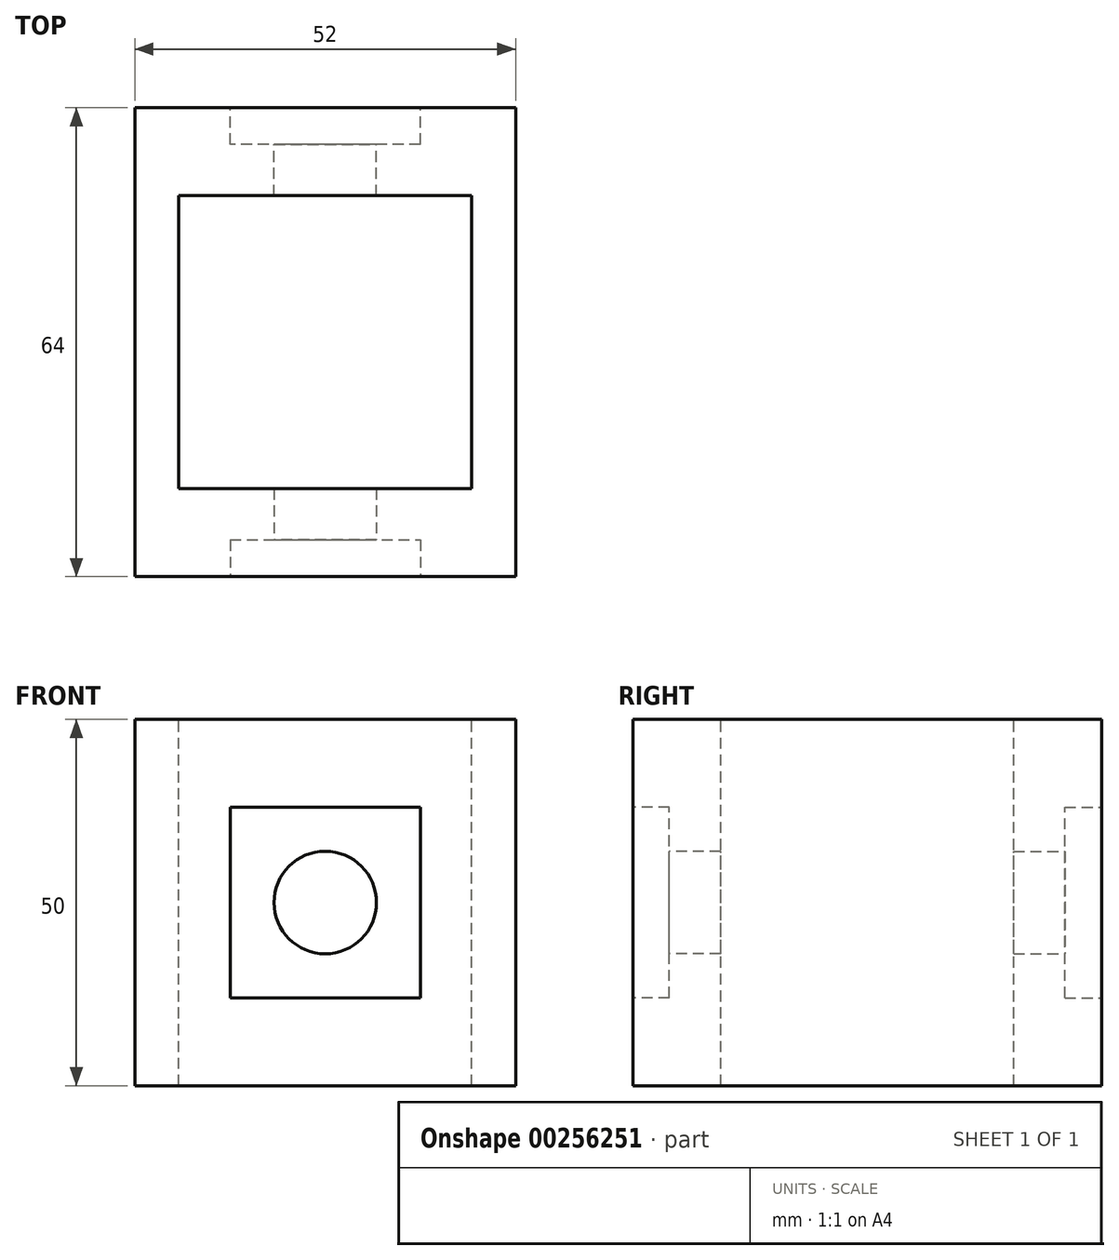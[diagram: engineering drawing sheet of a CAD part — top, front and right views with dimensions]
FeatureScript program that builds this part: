
annotation { "Feature Type Name" : "Feature", "Feature Type Description" : "" }
export const myFeature = defineFeature(function(context is Context, id is Id, definition is map)
    precondition{}
    {
        {
            var Q0;
            Q0=qCreatedBy(makeId("Top.planeOp"),FACE);
            var sketch = newSketch(context, id + "F0", { "sketchPlane" : qUnion([Q0])});
            skLineSegment(sketch, "E0.bottom", {"start": v(0, 0) * mm, "end": v(52, 0) * mm});
            skLineSegment(sketch, "E0.top", {"start": v(0, 64) * mm, "end": v(52, 64) * mm});
            skLineSegment(sketch, "E0.left", {"start": v(0, 0) * mm, "end": v(0, 64) * mm});
            skLineSegment(sketch, "E0.right", {"start": v(52, 0) * mm, "end": v(52, 64) * mm});
            skSolve(sketch);
        }
        {
            var Q0;
            Q0=makeQuery(id+"F0.imprint","IMPRINT",FACE,{"disambiguationData":[TD([[makeQuery(id+"F0.imprint","IMPRINT",EDGE,{"derivedFrom":sQuery(id+"F0.wireOp",EDGE,"E0.bottom")}),1.0]])]});
            extrude(context, id + "F1", {"entities" : qUnion([Q0]), "depth" : 50 * mm});
        }
        {
            var Q0;
            Q0=makeQuery(id+"F1.opExtrude","CAP_FACE",FACE,{"disambiguationData":[OSD([sQuery(id+"F0.wireOp",EDGE,"E0.bottom"),sQuery(id+"F0.wireOp",EDGE,"E0.top"),sQuery(id+"F0.wireOp",EDGE,"E0.left"),sQuery(id+"F0.wireOp",EDGE,"E0.right")])],"isStart":false});
            var sketch = newSketch(context, id + "F2", { "sketchPlane" : qUnion([Q0])});
            skLineSegment(sketch, "E1.bottom", {"start": v(6, 52) * mm, "end": v(46, 52) * mm});
            skLineSegment(sketch, "E1.top", {"start": v(6, 12) * mm, "end": v(46, 12) * mm});
            skLineSegment(sketch, "E1.left", {"start": v(6, 52) * mm, "end": v(6, 12) * mm});
            skLineSegment(sketch, "E1.right", {"start": v(46, 52) * mm, "end": v(46, 12) * mm});
            skSolve(sketch);
        }
        {
            var Q0;
            Q0=makeQuery(id+"F2.imprint","IMPRINT",FACE,{"disambiguationData":[TD([[makeQuery(id+"F2.imprint","IMPRINT",EDGE,{"derivedFrom":sQuery(id+"F2.wireOp",EDGE,"E1.bottom")}),-1.0]])]});
            extrude(context, id + "F3", {"entities" : qUnion([Q0]), "operationType" : NewBodyOperationType.REMOVE, "oppositeDirection" : true, "depth" : 50 * mm});
        }
        {
            var Q0;
            Q0=makeQuery(id+"F1.opExtrude","SWEPT_FACE",FACE,{"disambiguationData":[OSD([sQuery(id+"F0.wireOp",EDGE,"E0.bottom")])]});
            var sketch = newSketch(context, id + "F4", { "sketchPlane" : qUnion([Q0])});
            skLineSegment(sketch, "E2.bottom", {"start": v(13, 12) * mm, "end": v(39, 12) * mm});
            skLineSegment(sketch, "E2.top", {"start": v(13, 38) * mm, "end": v(39, 38) * mm});
            skLineSegment(sketch, "E2.left", {"start": v(13, 12) * mm, "end": v(13, 38) * mm});
            skLineSegment(sketch, "E2.right", {"start": v(39, 12) * mm, "end": v(39, 38) * mm});
            skSolve(sketch);
        }
        {
            var Q0;
            Q0=makeQuery(id+"F4.imprint","IMPRINT",FACE,{"disambiguationData":[TD([[makeQuery(id+"F4.imprint","IMPRINT",EDGE,{"derivedFrom":sQuery(id+"F4.wireOp",EDGE,"E2.bottom")}),1.0]])]});
            extrude(context, id + "F5", {"entities" : qUnion([Q0]), "operationType" : NewBodyOperationType.REMOVE, "oppositeDirection" : true, "depth" : 5 * mm});
        }
        {
            var Q0;
            Q0=makeQuery(id+"F5.boolean.opBoolean","COPY",FACE,{"derivedFrom":makeQuery(id+"F5.opExtrude","CAP_FACE",FACE,{"disambiguationData":[OSD([sQuery(id+"F4.wireOp",EDGE,"E2.bottom"),sQuery(id+"F4.wireOp",EDGE,"E2.top"),sQuery(id+"F4.wireOp",EDGE,"E2.left"),sQuery(id+"F4.wireOp",EDGE,"E2.right")])],"isStart":false})});
            var sketch = newSketch(context, id + "F6", { "sketchPlane" : qUnion([Q0])});
            skCircle(sketch, "E3", {"center": v(26, 25) * mm, "radius": 7 * mm});
            skPoint(sketch, "E3.centerSnap0", {"position": v(13, 25) * mm});
            skPoint(sketch, "E3.centerSnap1", {"position": v(26, 38) * mm});
            skSolve(sketch);
        }
        {
            var Q0;
            Q0=makeQuery(id+"F6.imprint","IMPRINT",FACE,{"disambiguationData":[TD([[makeQuery(id+"F6.imprint","IMPRINT",EDGE,{"derivedFrom":sQuery(id+"F6.wireOp",EDGE,"E3")}),1.0]])]});
            extrude(context, id + "F7", {"entities" : qUnion([Q0]), "operationType" : NewBodyOperationType.REMOVE, "oppositeDirection" : true, "depth" : 40 * mm});
        }
        {
            var Q0;
            Q0=makeQuery(id+"F1.opExtrude","SWEPT_FACE",FACE,{"disambiguationData":[OSD([sQuery(id+"F0.wireOp",EDGE,"E0.top")])]});
            var sketch = newSketch(context, id + "F8", { "sketchPlane" : qUnion([Q0])});
            skLineSegment(sketch, "E4.bottom", {"start": v(-39, 12) * mm, "end": v(-13, 12) * mm});
            skLineSegment(sketch, "E4.top", {"start": v(-39, 38) * mm, "end": v(-13, 38) * mm});
            skLineSegment(sketch, "E4.left", {"start": v(-39, 12) * mm, "end": v(-39, 38) * mm});
            skLineSegment(sketch, "E4.right", {"start": v(-13, 12) * mm, "end": v(-13, 38) * mm});
            skSolve(sketch);
        }
        {
            var Q0;
            Q0=makeQuery(id+"F8.imprint","IMPRINT",FACE,{"disambiguationData":[TD([[makeQuery(id+"F8.imprint","IMPRINT",EDGE,{"derivedFrom":sQuery(id+"F8.wireOp",EDGE,"E4.bottom")}),1.0]])]});
            extrude(context, id + "F9", {"entities" : qUnion([Q0]), "operationType" : NewBodyOperationType.REMOVE, "oppositeDirection" : true, "depth" : 5 * mm});
        }
        {
            var Q0;
            Q0=makeQuery(id+"F9.boolean.opBoolean","COPY",FACE,{"derivedFrom":makeQuery(id+"F9.opExtrude","CAP_FACE",FACE,{"disambiguationData":[OSD([sQuery(id+"F8.wireOp",EDGE,"E4.bottom"),sQuery(id+"F8.wireOp",EDGE,"E4.top"),sQuery(id+"F8.wireOp",EDGE,"E4.left"),sQuery(id+"F8.wireOp",EDGE,"E4.right")])],"isStart":false})});
            var sketch = newSketch(context, id + "F10", { "sketchPlane" : qUnion([Q0])});
            skCircle(sketch, "E5", {"center": v(-26, 25) * mm, "radius": 7 * mm});
            skPoint(sketch, "E5.centerSnap0", {"position": v(-26, 38) * mm});
            skPoint(sketch, "E5.centerSnap1", {"position": v(-39, 25) * mm});
            skSolve(sketch);
        }
        {
            var Q0;
            Q0=makeQuery(id+"F10.imprint","IMPRINT",FACE,{"disambiguationData":[TD([[makeQuery(id+"F10.imprint","IMPRINT",EDGE,{"derivedFrom":sQuery(id+"F10.wireOp",EDGE,"E5")}),1.0]])]});
            extrude(context, id + "F11", {"entities" : qUnion([Q0]), "operationType" : NewBodyOperationType.REMOVE, "oppositeDirection" : true, "depth" : 25 * mm});
        }
    });
